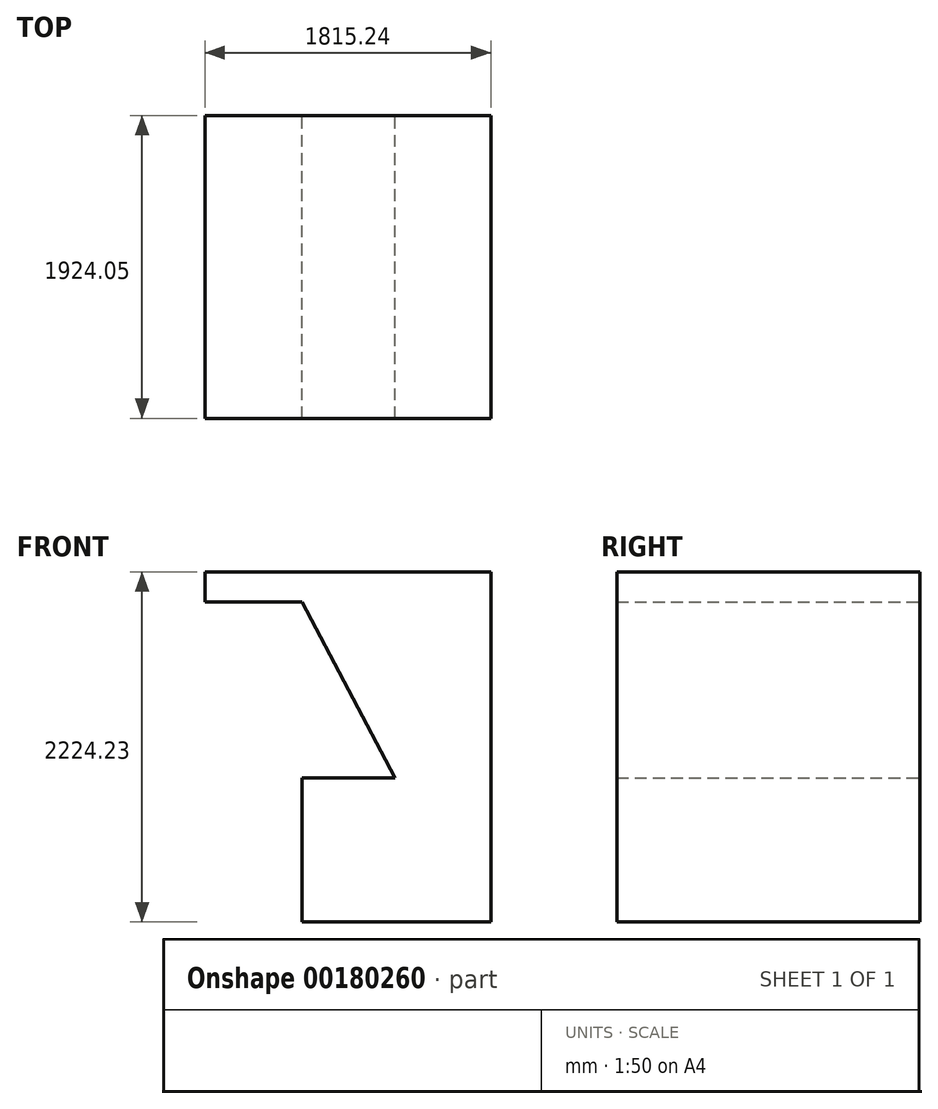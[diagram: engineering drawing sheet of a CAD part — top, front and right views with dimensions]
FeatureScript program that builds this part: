
annotation { "Feature Type Name" : "Feature", "Feature Type Description" : "" }
export const myFeature = defineFeature(function(context is Context, id is Id, definition is map)
    precondition{}
    {
        {
            var Q0;
            Q0=qCreatedBy(makeId("Front.planeOp"),FACE);
            var sketch = newSketch(context, id + "F0", { "sketchPlane" : qUnion([Q0])});
            skLineSegment(sketch, "E0.top", {"start": v(0, 914.4) * mm, "end": v(590.55, 914.4) * mm});
            skLineSegment(sketch, "E0.left", {"start": v(0, 0) * mm, "end": v(0, 914.4) * mm});
            skLineSegment(sketch, "E1", {"start": v(590.55, 914.4) * mm, "end": v(0, 2032) * mm});
            skLineSegment(sketch, "E2", {"start": v(1198.51, 2224.23) * mm, "end": v(1198.51, 0) * mm});
            skLineSegment(sketch, "E3", {"start": v(1198.51, 0) * mm, "end": v(0, 0) * mm});
            skLineSegment(sketch, "E4", {"start": v(0, 2032) * mm, "end": v(-616.73, 2032) * mm});
            skLineSegment(sketch, "E5", {"start": v(-616.73, 2032) * mm, "end": v(-616.73, 2224.23) * mm});
            skLineSegment(sketch, "E6", {"start": v(-616.73, 2224.23) * mm, "end": v(1198.51, 2224.23) * mm});
            skSolve(sketch);
        }
        {
            var Q0;
            Q0 = qSketchRegion(id + "F0", true);
            extrude(context, id + "F1", {"entities" : qUnion([Q0]), "depth" : 1924.05 * mm});
        }
    });
